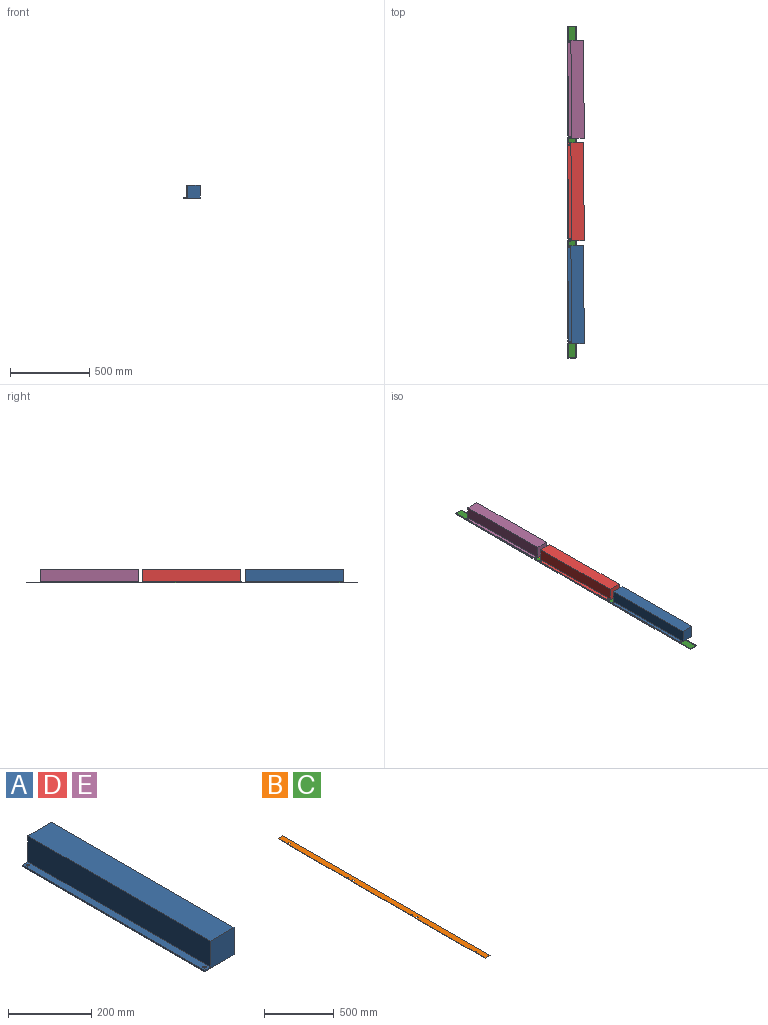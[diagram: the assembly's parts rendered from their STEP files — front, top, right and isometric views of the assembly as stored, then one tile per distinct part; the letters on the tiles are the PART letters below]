
ASSEMBLY  parts=5 mates=3
PART A: 10 faces, bbox 100x620x80 mm
  f0: plane 620x4mm, normal (-1,0,0), area 2480mm2, adj f1,f5,f6,f7
  f1: plane 620x100mm, normal (0,0,-1), area 61899.5mm2, adj f0,f2,f6,f7,f8,f9
  f2: plane 620x80mm, normal (1,0,0), area 49600mm2, adj f1,f3,f6,f7
  f3: plane 620x80mm, normal (0,0,1), area 49600mm2, adj f2,f4,f6,f7
  f4: plane 620x76mm, normal (-1,0,0), area 47120mm2, adj f3,f5,f6,f7
  f5: plane 620x20mm, normal (0,0,1), area 12299.5mm2, adj f0,f4,f6,f7,f8,f9
  f6: plane 100x80mm, normal (0,-1,0), area 6480mm2, adj f0,f1,f2,f3,f4,f5
  f7: plane 100x80mm, normal (0,1,0), area 6480mm2, adj f0,f1,f2,f3,f4,f5
  f8: cylinder r=4mm len=8mm, axis (0,0,1), area 100.5mm2, adj f1,f5
  f9: cylinder r=4mm len=8mm, axis (0,0,1), area 100.5mm2, adj f1,f5
PART B: 21 faces, bbox 50x2100x3 mm
  f0: plane 635x3mm, normal (-1,0,0), area 1905mm2, adj f3,f4,f15,f20
  f1: plane 635x3mm, normal (-1,0,0), area 1905mm2, adj f3,f4,f12,f17
  f2: plane 92.5x3mm, normal (-1,0,0), area 277.5mm2, adj f3,f4,f8,f14
  f3: plane 2100x50mm, normal (0,0,-1), area 104061.7mm2, adj f0,f1,f2,f5,f6,f7,f8,f9
  f4: plane 2100x50mm, normal (0,0,1), area 104061.7mm2, adj f0,f1,f2,f5,f6,f7,f8,f9
  f5: plane 2100x3mm, normal (1,0,0), area 6300mm2, adj f3,f4,f7,f8
  f6: plane 692.5x3mm, normal (-1,0,0), area 2077.5mm2, adj f3,f4,f7,f18
  f7: plane 50x3mm, normal (0,-1,0), area 150mm2, adj f3,f4,f5,f6
  f8: plane 50x3mm, normal (0,1,0), area 150mm2, adj f2,f3,f4,f5
  f9: cylinder r=4mm len=8mm, axis (0,0,1), area 75.4mm2, adj f3,f4
  f10: cylinder r=4mm len=8mm, axis (0,0,1), area 75.4mm2, adj f3,f4
  f11: cylinder r=4mm len=8mm, axis (0,0,1), area 75.4mm2, adj f3,f4
  f12: plane 17.5x3mm, normal (0,1,0), area 52.5mm2, adj f1,f3,f4,f13
  f13: plane 15x3mm, normal (-1,0,0), area 45mm2, adj f3,f4,f12,f14
  f14: plane 17.5x3mm, normal (0,-1,0), area 52.5mm2, adj f2,f3,f4,f13
  f15: plane 17.5x3mm, normal (0,1,0), area 52.5mm2, adj f0,f3,f4,f16
  f16: plane 15x3mm, normal (-1,0,0), area 45mm2, adj f3,f4,f15,f17
  f17: plane 17.5x3mm, normal (0,-1,0), area 52.5mm2, adj f1,f3,f4,f16
  f18: plane 17.5x3mm, normal (0,1,0), area 52.5mm2, adj f3,f4,f6,f19
  f19: plane 15x3mm, normal (-1,0,0), area 45mm2, adj f3,f4,f18,f20
  f20: plane 17.5x3mm, normal (0,-1,0), area 52.5mm2, adj f0,f3,f4,f19
PART C: same geometry as B
PART D: same geometry as A
PART E: same geometry as A
PLACE A rot(axis=(0,0,1),0.4deg) t=(-515.51,-950.52,-268.2)mm
PLACE B t=(-424.1,439.57,-271.2)mm fixed
PLACE C rot(axis=(1,0,0),180deg) t=(-428.48,-1660.45,-268.2)mm
PLACE D rot(axis=(0,0,1),0.4deg) t=(-515.51,-300.52,-268.2)mm
PLACE E rot(axis=(0,0,1),0.4deg) t=(-515.51,349.48,-268.2)mm
MATE revolute A.f9 <-> B.f11  axis (0,0,-1) through (-501.06,-1560.43,-268.2)mm
MATE revolute C.f11 <-> E.f8  axis (0,0,1) through (-505.44,339.55,-268.2)mm
MATE parallel B.f5 <-> C.f6  axis (1,0,0) through (-461.06,-610.43,-269.7)mm
